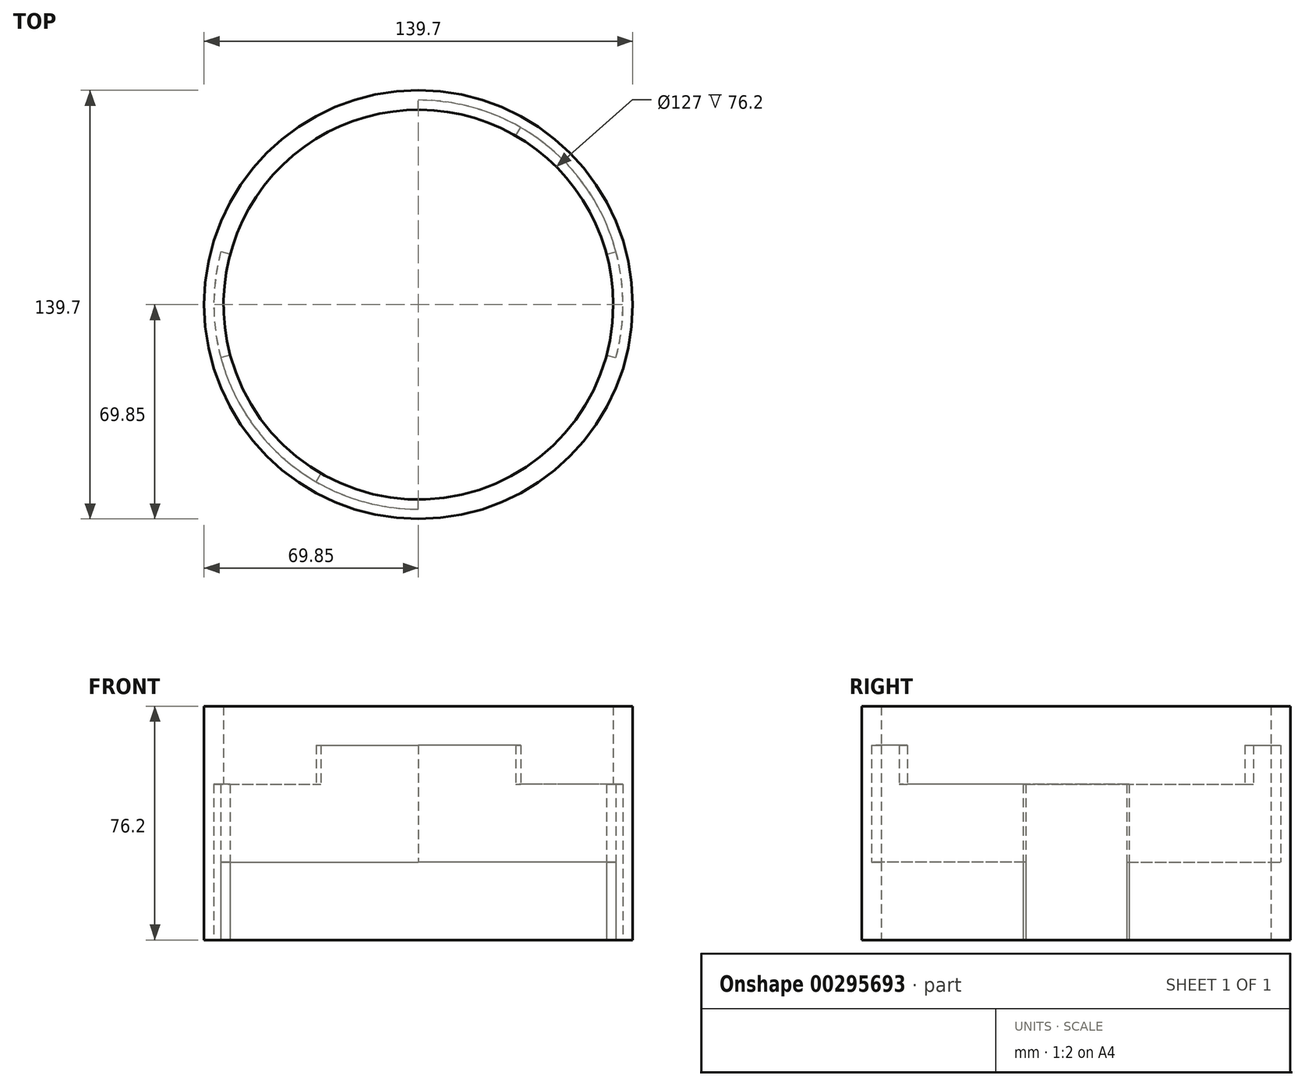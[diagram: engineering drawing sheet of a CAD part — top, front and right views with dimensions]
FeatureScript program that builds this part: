
annotation { "Feature Type Name" : "Feature", "Feature Type Description" : "" }
export const myFeature = defineFeature(function(context is Context, id is Id, definition is map)
    precondition{}
    {
        {
            var Q0;
            Q0=qCreatedBy(makeId("Top.planeOp"),FACE);
            var sketch = newSketch(context, id + "F0", { "sketchPlane" : qUnion([Q0])});
            skCircle(sketch, "E0", {"center": v(0, 0) * mm, "radius": 63.5 * mm});
            skCircle(sketch, "E1", {"center": v(0, 0) * mm, "radius": 66.68 * mm});
            skLineSegment(sketch, "E2", {"start": v(-61.34, -16.44) * mm, "end": v(-64.4, -17.26) * mm});
            skLineSegment(sketch, "E3.MirrorCS", {"start": v(-61.34, 16.44) * mm, "end": v(-64.4, 17.26) * mm});
            skLineSegment(sketch, "E4.MirrorCS", {"start": v(61.34, -16.44) * mm, "end": v(64.4, -17.26) * mm});
            skLineSegment(sketch, "E5.MirrorCS", {"start": v(61.34, 16.44) * mm, "end": v(64.4, 17.26) * mm});
            skCircle(sketch, "E6", {"center": v(0, 0) * mm, "radius": 69.85 * mm});
            skLineSegment(sketch, "E7", {"start": v(0, -66.68) * mm, "end": v(0, -63.5) * mm});
            skLineSegment(sketch, "E8", {"start": v(0, 63.5) * mm, "end": v(0, 66.68) * mm});
            skLineSegment(sketch, "E9", {"start": v(-33.34, -57.74) * mm, "end": v(-31.75, -55) * mm});
            skLineSegment(sketch, "E10.trimOffspring", {"start": v(31.75, 55) * mm, "end": v(33.34, 57.74) * mm});
            skSolve(sketch);
        }
        {
            var Q0;
            Q0=makeQuery(id+"F0.imprint","IMPRINT",FACE,{"disambiguationData":[TD([[makeQuery(id+"F0.imprint","IMPRINT",EDGE,{"derivedFrom":sQuery(id+"F0.wireOp",EDGE,"E6")}),1.0]])]});
            var Q1;
            {var subQ0=sQuery(id+"F0.wireOp",EDGE,"E2");Q1=makeQuery(id+"F0.imprint","IMPRINT",FACE,{"disambiguationData":[TD([[makeQuery(id+"F0.imprint","IMPRINT",EDGE,{"derivedFrom":subQ0}),1.0]])]});}
            var Q2;
            {var subQ0=sQuery(id+"F0.wireOp",EDGE,"E3.MirrorCS");Q2=makeQuery(id+"F0.imprint","IMPRINT",FACE,{"disambiguationData":[TD([[makeQuery(id+"F0.imprint","IMPRINT",EDGE,{"derivedFrom":subQ0}),-1.0]])]});}
            var Q3;
            {var subQ0=sQuery(id+"F0.wireOp",EDGE,"E2");Q3=makeQuery(id+"F0.imprint","IMPRINT",FACE,{"disambiguationData":[TD([[makeQuery(id+"F0.imprint","IMPRINT",EDGE,{"derivedFrom":subQ0}),-1.0]])]});}
            var Q4;
            {var subQ0=sQuery(id+"F0.wireOp",EDGE,"E4.MirrorCS");Q4=makeQuery(id+"F0.imprint","IMPRINT",FACE,{"disambiguationData":[TD([[makeQuery(id+"F0.imprint","IMPRINT",EDGE,{"derivedFrom":subQ0}),1.0]])]});}
            var Q5;
            {var subQ0=sQuery(id+"F0.wireOp",EDGE,"E5.MirrorCS");Q5=makeQuery(id+"F0.imprint","IMPRINT",FACE,{"disambiguationData":[TD([[makeQuery(id+"F0.imprint","IMPRINT",EDGE,{"derivedFrom":subQ0}),1.0]])]});}
            var Q6;
            {var subQ0=sQuery(id+"F0.wireOp",EDGE,"E4.MirrorCS");Q6=makeQuery(id+"F0.imprint","IMPRINT",FACE,{"disambiguationData":[TD([[makeQuery(id+"F0.imprint","IMPRINT",EDGE,{"derivedFrom":subQ0}),-1.0]])]});}
            var Q7;
            {var subQ0=sQuery(id+"F0.wireOp",EDGE,"E7");Q7=makeQuery(id+"F0.imprint","IMPRINT",FACE,{"disambiguationData":[TD([[makeQuery(id+"F0.imprint","IMPRINT",EDGE,{"derivedFrom":subQ0}),1.0]])]});}
            var Q8;
            {var subQ0=sQuery(id+"F0.wireOp",EDGE,"E8");Q8=makeQuery(id+"F0.imprint","IMPRINT",FACE,{"disambiguationData":[TD([[makeQuery(id+"F0.imprint","IMPRINT",EDGE,{"derivedFrom":subQ0}),-1.0]])]});}
            extrude(context, id + "F1", {"entities" : qUnion([Q0, Q1, Q2, Q3, Q4, Q5, Q6, Q7, Q8]), "depth" : 76.2 * mm});
        }
        {
            var Q0;
            {var subQ0=sQuery(id+"F0.wireOp",EDGE,"E2");Q0=makeQuery(id+"F0.imprint","IMPRINT",FACE,{"disambiguationData":[TD([[makeQuery(id+"F0.imprint","IMPRINT",EDGE,{"derivedFrom":subQ0}),-1.0]])]});}
            var Q1;
            {var subQ0=sQuery(id+"F0.wireOp",EDGE,"E4.MirrorCS");Q1=makeQuery(id+"F0.imprint","IMPRINT",FACE,{"disambiguationData":[TD([[makeQuery(id+"F0.imprint","IMPRINT",EDGE,{"derivedFrom":subQ0}),1.0]])]});}
            var Q2;
            {var subQ0=sQuery(id+"F0.wireOp",EDGE,"E2");Q2=makeQuery(id+"F0.imprint","IMPRINT",FACE,{"disambiguationData":[TD([[makeQuery(id+"F0.imprint","IMPRINT",EDGE,{"derivedFrom":subQ0}),1.0]])]});}
            var Q3;
            {var subQ0=sQuery(id+"F0.wireOp",EDGE,"E5.MirrorCS");Q3=makeQuery(id+"F0.imprint","IMPRINT",FACE,{"disambiguationData":[TD([[makeQuery(id+"F0.imprint","IMPRINT",EDGE,{"derivedFrom":subQ0}),1.0]])]});}
            extrude(context, id + "F2", {"entities" : qUnion([Q0, Q1, Q2, Q3]), "operationType" : NewBodyOperationType.REMOVE, "depth" : 50.8 * mm});
        }
        {
            var Q0;
            {var subQ0=sQuery(id+"F0.wireOp",EDGE,"E7");Q0=makeQuery(id+"F0.imprint","IMPRINT",FACE,{"disambiguationData":[TD([[makeQuery(id+"F0.imprint","IMPRINT",EDGE,{"derivedFrom":subQ0}),1.0]])]});}
            var Q1;
            {var subQ0=sQuery(id+"F0.wireOp",EDGE,"E8");Q1=makeQuery(id+"F0.imprint","IMPRINT",FACE,{"disambiguationData":[TD([[makeQuery(id+"F0.imprint","IMPRINT",EDGE,{"derivedFrom":subQ0}),-1.0]])]});}
            extrude(context, id + "F3", {"entities" : qUnion([Q0, Q1]), "operationType" : NewBodyOperationType.REMOVE, "depth" : 63.5 * mm});
        }
        {
            var Q0;
            {var subQ0=sQuery(id+"F0.wireOp",EDGE,"E2");Q0=makeQuery(id+"F0.imprint","IMPRINT",FACE,{"disambiguationData":[TD([[makeQuery(id+"F0.imprint","IMPRINT",EDGE,{"derivedFrom":subQ0}),1.0]])]});}
            var Q1;
            {var subQ0=sQuery(id+"F0.wireOp",EDGE,"E7");Q1=makeQuery(id+"F0.imprint","IMPRINT",FACE,{"disambiguationData":[TD([[makeQuery(id+"F0.imprint","IMPRINT",EDGE,{"derivedFrom":subQ0}),1.0]])]});}
            var Q2;
            {var subQ0=sQuery(id+"F0.wireOp",EDGE,"E5.MirrorCS");Q2=makeQuery(id+"F0.imprint","IMPRINT",FACE,{"disambiguationData":[TD([[makeQuery(id+"F0.imprint","IMPRINT",EDGE,{"derivedFrom":subQ0}),1.0]])]});}
            var Q3;
            {var subQ0=sQuery(id+"F0.wireOp",EDGE,"E8");Q3=makeQuery(id+"F0.imprint","IMPRINT",FACE,{"disambiguationData":[TD([[makeQuery(id+"F0.imprint","IMPRINT",EDGE,{"derivedFrom":subQ0}),-1.0]])]});}
            extrude(context, id + "F4", {"entities" : qUnion([Q0, Q1, Q2, Q3]), "operationType" : NewBodyOperationType.ADD, "depth" : 25.4 * mm});
        }
    });
